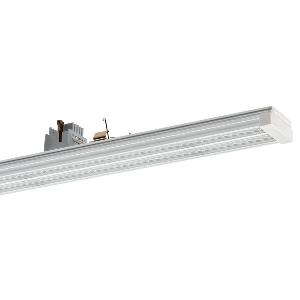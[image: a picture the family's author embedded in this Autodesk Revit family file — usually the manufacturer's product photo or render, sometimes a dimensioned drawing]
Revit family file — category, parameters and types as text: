
# Revit family: conveo_-_cvg_15000_840_w-l_ea_5_226848359-00804974_f898
name_source: partatom
category: Lighting Fixtures
units: mm (PartAtom-declared; Revit-internal decimal feet)

## family parameters
Cut with Voids When Loaded = No
Host = Face
Light Source = No
Part Type = Normal
Room Calculation Point = No
Round Connector Dimension = Use Diameter
Shared = No

## types (1)
- CONVEO - CVG 15000/840/W-L/EA/5 (1 x LED, 14800 lm, 4000K)
    Apparent Load = 86 VA
    Approval mark = CE
    CIE Flux Codes = 85 97 99 100 100
    Color Rendering = 80-89
    Color Temperature = 4000K
    Control Gear = Electronic ballast
    Default Elevation = 1800 mm
    Description = CVG 15000/840/W-L/EA/5|Continuous-row system|light source: LED|work equipment: Electronic ballast|connected load: 220-240 V, 50-60 Hz|Power consumption: approx. 86 W|luminous flux: 14800 lm|luminous efficacy: 172 lm/W|colour temperature: Cold white, ca. 4000 K|color rendering index (CRI): >= 80|chromaticity tolerance:  3 SDCM|System of protection: IP 54|class of protection: I|technology: Switchable|luminaire body|material: Aluminium|surface: Powder coatet|colour: White|lamp cover: Acrylic (PMMA), Satine|weight (net): approx. 2.2 kg|Fastening: Available separately|maximum ambient temperature: 41 ░C|glare control: Lens optics|Approval mark: VDE - ENEC|
    Frequency = 50 Hz
    Height = 70 mm
    Lamp = 1 x LED
    Lamp Light Flux = 14800 lm
    Lamp count = 1
    Length = 1500 mm
    Luminous efficacy = 172 lm/W
    Manufacturer = Waldmann
    ModVariant = No
    Model = 226848359-00804974
    Mounting Place = Ceiling
    Mounting Type = Pendant
    Number of Poles = 1
    OnlyDefault = Yes
    Power Factor = 1
    Product Name = CONVEO - CVG 15000/840/W-L/EA/5
    Product group = Continuous-row system (industry)
    ProductGroupID = 301
    Protection Class = Protection class I
    Protection Degree = IP 54
    RLX_Detail_Level = 1
    RlxData = <blob elided: 135813 chars, md5=dbe238b4>
    Socket = socket
    Standby Power = 0 W
    System Light Flux = 14800 lm
    System Power = 86 W
    Type Comments = Product without accessories
    Type Image = 226848359-00804974-2l5.jpg
    URL = http://relux.com
    VarID = ---
    Voltage = 230 V
    Voltage Range = 220-240 V
    Weight = 0.00 kg
    Width = 64 mm

## geometry (parser evidence)
native form markers: Blend x4, Sweep x10
no freeform markers — native parametric forms only
